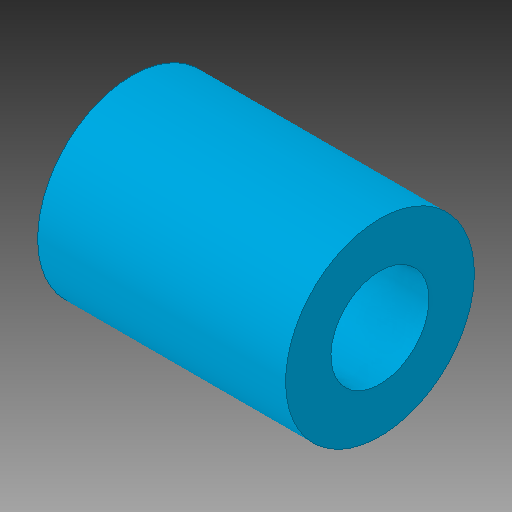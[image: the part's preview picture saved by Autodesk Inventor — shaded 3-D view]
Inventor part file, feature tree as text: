
AUTODESK INVENTOR PART (.ipt)
format: ipt  version: 2017 SP1 (Build 210196100, 196)  size: 100,352 bytes
history: native  units: in
note: dims shown in document units (in); Inventor stores cm internally (conversion verified against a paired STEP export)
features: extrude x1, sketch x1
ambient origin geometry x8: Origin, YZ Plane, XZ Plane, XY Plane, X Axis, Y Axis, Z Axis, Center Point
bodies: Solid1 (feature_tree)
feature tree (2):
  extrude  "Extrusion1"  Depth=0.657in
  sketch  "Sketch1"  dims[d0=0.26in d1=0.5in d2=0.657in d3=0.0in]
